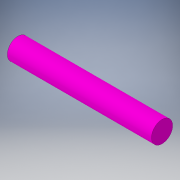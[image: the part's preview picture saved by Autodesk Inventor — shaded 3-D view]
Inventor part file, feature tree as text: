
AUTODESK INVENTOR PART (.ipt)
format: ipt  version: 2017 (Build 210142000, 142)  size: 88,576 bytes
history: native  units: in
note: dims shown in document units (in); Inventor stores cm internally (conversion verified against a paired STEP export)
features: extrude x1, sketch x1
ambient origin geometry x8: Origin, YZ Plane, XZ Plane, XY Plane, X Axis, Y Axis, Z Axis, Center Point
bodies: Solid1 (feature_tree)
feature tree (2):
  extrude  "Extrusion1"  Depth=2.125in TaperAngle=0.0deg
  sketch  "Sketch1"  dims[d0=0.3125in d1=2.125in d2=0.0in]
